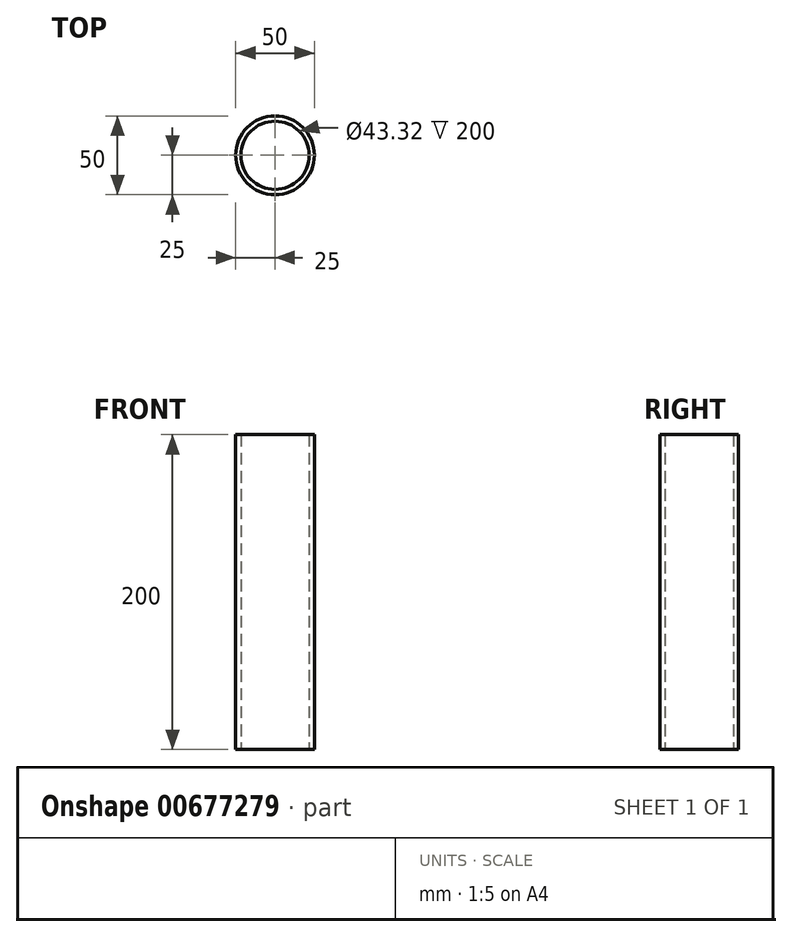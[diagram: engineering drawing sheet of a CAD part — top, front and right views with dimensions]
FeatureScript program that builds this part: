
annotation { "Feature Type Name" : "Feature", "Feature Type Description" : "" }
export const myFeature = defineFeature(function(context is Context, id is Id, definition is map)
    precondition{}
    {
        {
            var Q0;
            Q0=qCreatedBy(makeId("Top.planeOp"),FACE);
            var sketch = newSketch(context, id + "F0", { "sketchPlane" : qUnion([Q0])});
            skCircle(sketch, "E0", {"center": v(0, 0) * mm, "radius": 25 * mm});
            skCircle(sketch, "E1", {"center": v(0, 0) * mm, "radius": 21.66 * mm});
            skSolve(sketch);
        }
        {
            var Q0;
            Q0=makeQuery(id+"F0.imprint","IMPRINT",FACE,{"disambiguationData":[TD([[makeQuery(id+"F0.imprint","IMPRINT",EDGE,{"derivedFrom":sQuery(id+"F0.wireOp",EDGE,"E1")}),1.0]])]});
            var sketch = newSketch(context, id + "F1", { "sketchPlane" : qUnion([Q0])});
            skSolve(sketch);
        }
        {
            var Q0;
            Q0 = qSketchRegion(id + "F1", true);
            var Q1;
            Q1=makeQuery(id+"F0.imprint","IMPRINT",FACE,{"disambiguationData":[TD([[makeQuery(id+"F0.imprint","IMPRINT",EDGE,{"derivedFrom":sQuery(id+"F0.wireOp",EDGE,"E0")}),1.0]])]});
            extrude(context, id + "F2", {"entities" : qUnion([Q0, Q1]), "depth" : 200 * mm, "offsetDistance" : 25.4 * mm});
        }
    });
